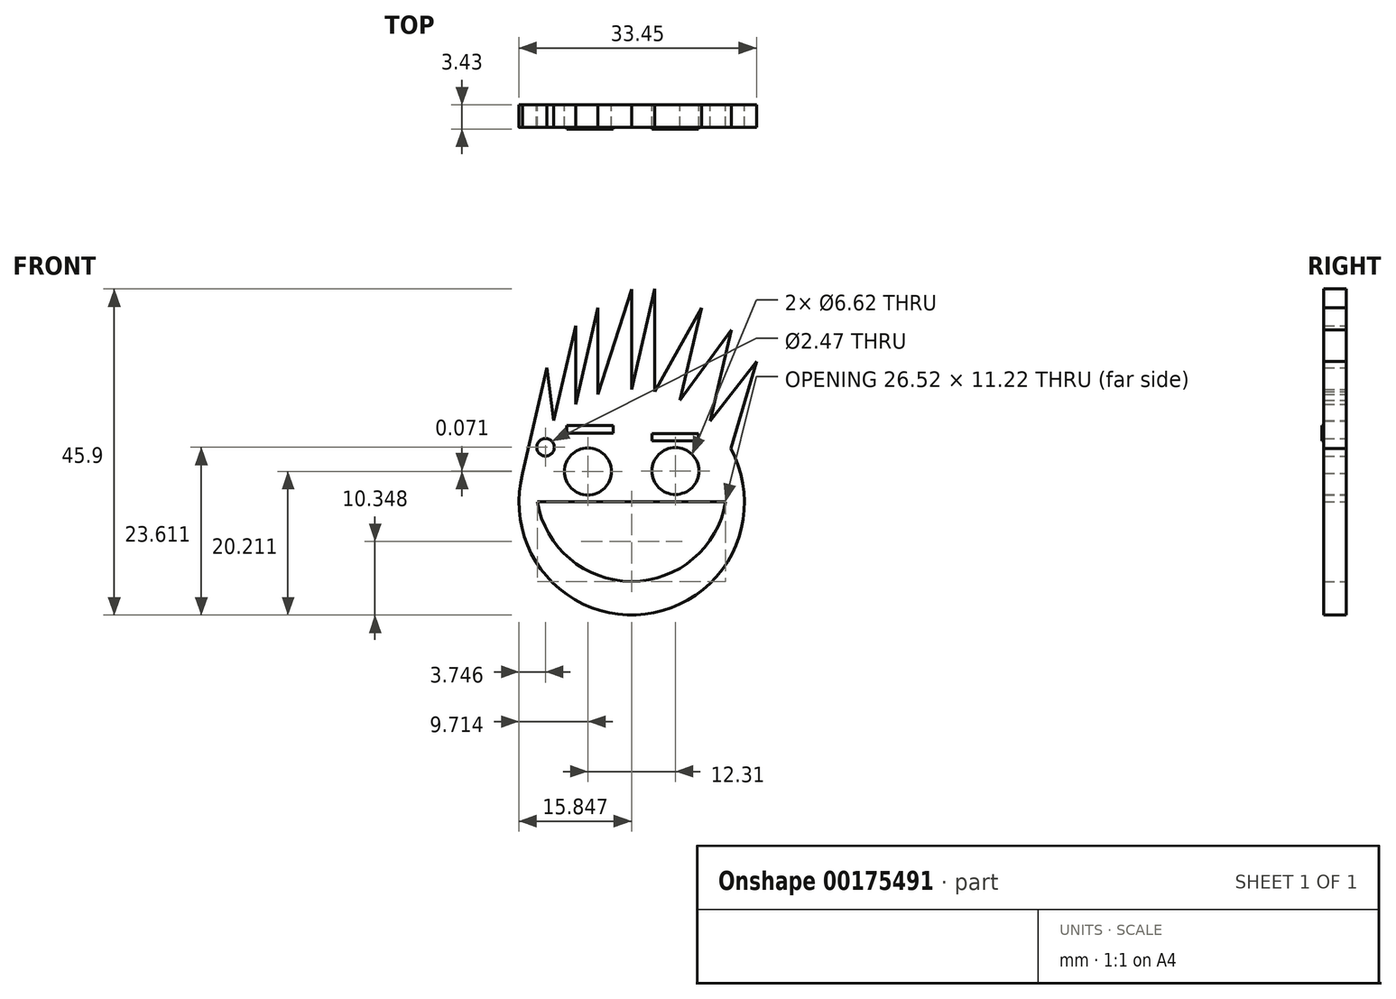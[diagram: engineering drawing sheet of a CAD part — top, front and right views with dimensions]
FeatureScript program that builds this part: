
annotation { "Feature Type Name" : "Feature", "Feature Type Description" : "" }
export const myFeature = defineFeature(function(context is Context, id is Id, definition is map)
    precondition{}
    {
        {
            var Q0;
            Q0=qCreatedBy(makeId("Front.planeOp"),FACE);
            var sketch = newSketch(context, id + "F0", { "sketchPlane" : qUnion([Q0])});
            skCircle(sketch, "E0", {"center": v(0, 0) * mm, "radius": 15.88 * mm});
            skLineSegment(sketch, "E1", {"start": v(-15.35, 4.06) * mm, "end": v(-11.92, 18.92) * mm});
            skLineSegment(sketch, "E2", {"start": v(-11.92, 18.92) * mm, "end": v(-10.95, 11.49) * mm});
            skPoint(sketch, "E2.endSnap0", {"position": v(-13.63, 11.49) * mm});
            skLineSegment(sketch, "E3", {"start": v(-10.95, 11.49) * mm, "end": v(-7.88, 24.84) * mm});
            skLineSegment(sketch, "E4", {"start": v(-7.88, 24.84) * mm, "end": v(-7.88, 13.78) * mm});
            skLineSegment(sketch, "E5", {"start": v(-7.88, 13.78) * mm, "end": v(-4.74, 27.4) * mm});
            skLineSegment(sketch, "E6", {"start": v(-4.74, 27.4) * mm, "end": v(-4.74, 15.15) * mm});
            skLineSegment(sketch, "E7", {"start": v(-4.74, 15.15) * mm, "end": v(0, 29.95) * mm});
            skLineSegment(sketch, "E8", {"start": v(0, 15.88) * mm, "end": v(3.26, 30.02) * mm});
            skLineSegment(sketch, "E9", {"start": v(3.26, 30.02) * mm, "end": v(3.26, 15.54) * mm});
            skLineSegment(sketch, "E10", {"start": v(3.26, 15.54) * mm, "end": v(9.83, 27.4) * mm});
            skLineSegment(sketch, "E11", {"start": v(9.83, 27.4) * mm, "end": v(6.82, 14.33) * mm});
            skLineSegment(sketch, "E12", {"start": v(6.82, 14.33) * mm, "end": v(14, 24.29) * mm});
            skLineSegment(sketch, "E13", {"start": v(14, 24.29) * mm, "end": v(11.04, 11.41) * mm});
            skLineSegment(sketch, "E14", {"start": v(0, 15.88) * mm, "end": v(0, 29.95) * mm});
            skLineSegment(sketch, "E15", {"start": v(17.58, 19.82) * mm, "end": v(13.95, 7.57) * mm});
            skLineSegment(sketch, "E16", {"start": v(11.04, 11.41) * mm, "end": v(17.58, 19.82) * mm});
            skSolve(sketch);
        }
        {
            var Q0;
            Q0=makeQuery(id+"F0.imprint","IMPRINT",FACE,{"disambiguationData":[TD([[makeQuery(id+"F0.imprint","IMPRINT",EDGE,{"derivedFrom":sQuery(id+"F0.wireOp",EDGE,"E0")}),1.0]])]});
            var sketch = newSketch(context, id + "F1", { "sketchPlane" : qUnion([Q0])});
            skCircle(sketch, "E17", {"center": v(-6.16, 4.33) * mm, "radius": 3.3 * mm});
            skCircle(sketch, "E18", {"center": v(6.15, 4.4) * mm, "radius": 3.3 * mm});
            skLineSegment(sketch, "E19.bottom", {"start": v(-9.13, 10.77) * mm, "end": v(-2.61, 10.77) * mm});
            skLineSegment(sketch, "E19.top", {"start": v(-9.13, 9.72) * mm, "end": v(-2.61, 9.72) * mm});
            skLineSegment(sketch, "E19.left", {"start": v(-9.13, 10.77) * mm, "end": v(-9.13, 9.72) * mm});
            skLineSegment(sketch, "E19.right", {"start": v(-2.61, 10.77) * mm, "end": v(-2.61, 9.72) * mm});
            skLineSegment(sketch, "E20.bottom", {"start": v(2.89, 9.68) * mm, "end": v(9.4, 9.68) * mm});
            skLineSegment(sketch, "E20.top", {"start": v(2.89, 8.63) * mm, "end": v(9.4, 8.63) * mm});
            skLineSegment(sketch, "E20.left", {"start": v(2.89, 9.68) * mm, "end": v(2.89, 8.63) * mm});
            skLineSegment(sketch, "E20.right", {"start": v(9.4, 9.68) * mm, "end": v(9.4, 8.63) * mm});
            skArc(sketch, "E21", {"start": v(-13.28, 0.08) * mm, "mid": v(-0.02, -11.14) * mm, "end": v(13.24, 0.08) * mm});
            skLineSegment(sketch, "E22", {"start": v(-13.28, 0.08) * mm, "end": v(13.24, 0.08) * mm});
            skCircle(sketch, "E23", {"center": v(-12.12, 7.73) * mm, "radius": 1.24 * mm});
            skSolve(sketch);
        }
        {
            var Q0;
            {var subQ0=sQuery(id+"F0.wireOp",EDGE,"E0");var subQ5=makeQuery(id+"F0.imprint","INTERSECT",VERTEX,{"derivedFrom":[subQ0,sQuery(id+"F0.wireOp",EDGE,"E1")]});Q0=makeQuery(id+"F0.imprint","IMPRINT",FACE,{"disambiguationData":[TD([[makeQuery(id+"F0.imprint","IMPRINT",EDGE,{"disambiguationData":[TD([[subQ5,-1.0]])],"derivedFrom":subQ0}),1.0]])]});}
            extrude(context, id + "F2", {"entities" : qUnion([Q0]), "depth" : 3.17 * mm});
        }
        {
            var Q0;
            Q0=makeQuery(id+"F1.imprint","IMPRINT",FACE,{"disambiguationData":[TD([[makeQuery(id+"F1.imprint","IMPRINT",EDGE,{"derivedFrom":sQuery(id+"F1.wireOp",EDGE,"E17")}),1.0]])]});
            var Q1;
            Q1=makeQuery(id+"F2.opExtrude","CAP_FACE",FACE,{"disambiguationData":[OSD([sQuery(id+"F0.wireOp",EDGE,"E0")])],"isStart":false});
            extrude(context, id + "F3", {"entities" : qUnion([Q0, Q1]), "operationType" : NewBodyOperationType.REMOVE, "endBound" : BoundingType.THROUGH_ALL, "depth" : 25.4 * mm});
        }
        {
            var Q0;
            Q0=makeQuery(id+"F1.imprint","IMPRINT",FACE,{"disambiguationData":[TD([[makeQuery(id+"F1.imprint","IMPRINT",EDGE,{"derivedFrom":sQuery(id+"F1.wireOp",EDGE,"E18")}),1.0]])]});
            extrude(context, id + "F4", {"entities" : qUnion([Q0]), "operationType" : NewBodyOperationType.REMOVE, "endBound" : BoundingType.THROUGH_ALL, "depth" : 25.4 * mm});
        }
        {
            var Q0;
            Q0=makeQuery(id+"F1.imprint","IMPRINT",FACE,{"disambiguationData":[TD([[makeQuery(id+"F1.imprint","IMPRINT",EDGE,{"derivedFrom":sQuery(id+"F1.wireOp",EDGE,"E21")}),1.0]])]});
            extrude(context, id + "F5", {"entities" : qUnion([Q0]), "operationType" : NewBodyOperationType.REMOVE, "endBound" : BoundingType.THROUGH_ALL, "depth" : 25.4 * mm});
        }
        {
            var Q0;
            Q0=makeQuery(id+"F1.imprint","IMPRINT",FACE,{"disambiguationData":[TD([[makeQuery(id+"F1.imprint","IMPRINT",EDGE,{"derivedFrom":sQuery(id+"F1.wireOp",EDGE,"E20.bottom")}),-1.0]])]});
            extrude(context, id + "F6", {"entities" : qUnion([Q0]), "operationType" : NewBodyOperationType.ADD, "depth" : 3.43 * mm});
        }
        {
            var Q0;
            {var subQ0=sQuery(id+"F0.wireOp",EDGE,"E1");Q0=makeQuery(id+"F0.imprint","IMPRINT",FACE,{"disambiguationData":[TD([[makeQuery(id+"F0.imprint","IMPRINT",EDGE,{"derivedFrom":subQ0}),-1.0]])]});}
            extrude(context, id + "F7", {"entities" : qUnion([Q0]), "operationType" : NewBodyOperationType.ADD, "depth" : 3.17 * mm});
        }
        {
            var Q0;
            {var subQ0=sQuery(id+"F0.wireOp",EDGE,"E3");Q0=makeQuery(id+"F0.imprint","IMPRINT",FACE,{"disambiguationData":[TD([[makeQuery(id+"F0.imprint","IMPRINT",EDGE,{"derivedFrom":subQ0}),-1.0]])]});}
            extrude(context, id + "F8", {"entities" : qUnion([Q0]), "operationType" : NewBodyOperationType.ADD, "depth" : 3.17 * mm});
        }
        {
            var Q0;
            {var subQ0=sQuery(id+"F0.wireOp",EDGE,"E5");Q0=makeQuery(id+"F0.imprint","IMPRINT",FACE,{"disambiguationData":[TD([[makeQuery(id+"F0.imprint","IMPRINT",EDGE,{"derivedFrom":subQ0}),-1.0]])]});}
            var sketch = newSketch(context, id + "F9", { "sketchPlane" : qUnion([Q0])});
            skSolve(sketch);
        }
        {
            var Q0;
            Q0 = qSketchRegion(id + "F9", true);
            var Q1;
            {var subQ0=sQuery(id+"F0.wireOp",EDGE,"E7");Q1=makeQuery(id+"F0.imprint","IMPRINT",FACE,{"disambiguationData":[TD([[makeQuery(id+"F0.imprint","IMPRINT",EDGE,{"derivedFrom":subQ0}),-1.0]])]});}
            var Q2;
            {var subQ0=sQuery(id+"F0.wireOp",EDGE,"E8");Q2=makeQuery(id+"F0.imprint","IMPRINT",FACE,{"disambiguationData":[TD([[makeQuery(id+"F0.imprint","IMPRINT",EDGE,{"derivedFrom":subQ0}),-1.0]])]});}
            var Q3;
            {var subQ0=sQuery(id+"F0.wireOp",EDGE,"E10");Q3=makeQuery(id+"F0.imprint","IMPRINT",FACE,{"disambiguationData":[TD([[makeQuery(id+"F0.imprint","IMPRINT",EDGE,{"derivedFrom":subQ0}),-1.0]])]});}
            var Q4;
            {var subQ0=sQuery(id+"F0.wireOp",EDGE,"E12");Q4=makeQuery(id+"F0.imprint","IMPRINT",FACE,{"disambiguationData":[TD([[makeQuery(id+"F0.imprint","IMPRINT",EDGE,{"derivedFrom":subQ0}),-1.0]])]});}
            var Q5;
            {var subQ2=sQuery(id+"F0.wireOp",EDGE,"E15");Q5=makeQuery(id+"F0.imprint","IMPRINT",FACE,{"disambiguationData":[TD([[makeQuery(id+"F0.imprint","IMPRINT",EDGE,{"derivedFrom":subQ2}),-1.0]])]});}
            var Q6;
            {var subQ0=sQuery(id+"F0.wireOp",EDGE,"E5");Q6=makeQuery(id+"F0.imprint","IMPRINT",FACE,{"disambiguationData":[TD([[makeQuery(id+"F0.imprint","IMPRINT",EDGE,{"derivedFrom":subQ0}),-1.0]])]});}
            extrude(context, id + "F10", {"entities" : qUnion([Q0, Q1, Q2, Q3, Q4, Q5, Q6]), "operationType" : NewBodyOperationType.ADD, "depth" : 3.17 * mm});
        }
        {
            var Q0;
            Q0=makeQuery(id+"F1.imprint","IMPRINT",FACE,{"disambiguationData":[TD([[makeQuery(id+"F1.imprint","IMPRINT",EDGE,{"derivedFrom":sQuery(id+"F1.wireOp",EDGE,"E23")}),1.0]])]});
            var Q1;
            {var subQ0=sQuery(id+"F0.wireOp",EDGE,"E0");Q1=makeQuery(id+"F10.boolean.opBoolean","MERGE",FACE,{"derivedFrom":[makeQuery(id+"F8.boolean.opBoolean","MERGE",FACE,{"derivedFrom":[makeQuery(id+"F7.boolean.opBoolean","MERGE",FACE,{"derivedFrom":[makeQuery(id+"F2.opExtrude","CAP_FACE",FACE,{"disambiguationData":[OSD([subQ0])],"isStart":false}),makeQuery(id+"F7.opExtrude","CAP_FACE",FACE,{"disambiguationData":[OSD([subQ0,sQuery(id+"F0.wireOp",EDGE,"E1"),sQuery(id+"F0.wireOp",EDGE,"E2")])],"isStart":false})]}),makeQuery(id+"F8.opExtrude","CAP_FACE",FACE,{"disambiguationData":[OSD([subQ0,sQuery(id+"F0.wireOp",EDGE,"E3"),sQuery(id+"F0.wireOp",EDGE,"E4")])],"isStart":false})]}),makeQuery(id+"F10.opExtrude","CAP_FACE",FACE,{"disambiguationData":[OSD([subQ0,sQuery(id+"F0.wireOp",EDGE,"E15"),sQuery(id+"F0.wireOp",EDGE,"E16")])],"isStart":false}),makeQuery(id+"F10.opExtrude","CAP_FACE",FACE,{"disambiguationData":[OSD([subQ0,sQuery(id+"F0.wireOp",EDGE,"E12"),sQuery(id+"F0.wireOp",EDGE,"E13")])],"isStart":false}),makeQuery(id+"F10.opExtrude","CAP_FACE",FACE,{"disambiguationData":[OSD([subQ0,sQuery(id+"F0.wireOp",EDGE,"E10"),sQuery(id+"F0.wireOp",EDGE,"E11")])],"isStart":false}),makeQuery(id+"F10.opExtrude","CAP_FACE",FACE,{"disambiguationData":[OSD([subQ0,sQuery(id+"F0.wireOp",EDGE,"E8"),sQuery(id+"F0.wireOp",EDGE,"E9")])],"isStart":false}),makeQuery(id+"F10.opExtrude","CAP_FACE",FACE,{"disambiguationData":[OSD([subQ0,sQuery(id+"F0.wireOp",EDGE,"E7"),sQuery(id+"F0.wireOp",EDGE,"E14")])],"isStart":false}),makeQuery(id+"F10.opExtrude","CAP_FACE",FACE,{"disambiguationData":[OSD([subQ0,sQuery(id+"F0.wireOp",EDGE,"E5"),sQuery(id+"F0.wireOp",EDGE,"E6")])],"isStart":false})]});}
            extrude(context, id + "F11", {"entities" : qUnion([Q0, Q1]), "operationType" : NewBodyOperationType.REMOVE, "endBound" : BoundingType.THROUGH_ALL, "depth" : 30.48 * mm});
        }
        {
            var Q0;
            Q0=makeQuery(id+"F1.imprint","IMPRINT",FACE,{"disambiguationData":[TD([[makeQuery(id+"F1.imprint","IMPRINT",EDGE,{"derivedFrom":sQuery(id+"F1.wireOp",EDGE,"E19.bottom")}),-1.0]])]});
            extrude(context, id + "F12", {"entities" : qUnion([Q0]), "operationType" : NewBodyOperationType.ADD, "depth" : 3.43 * mm});
        }
    });
